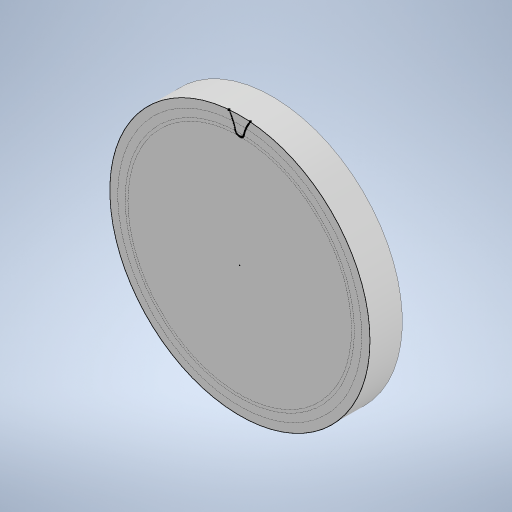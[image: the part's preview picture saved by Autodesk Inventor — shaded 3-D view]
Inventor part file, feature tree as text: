
AUTODESK INVENTOR PART (.ipt)
format: ipt  version: 2024 (Build 280153000, 153)  size: 217,088 bytes
history: native  units: mm
features: extrude x1
ambient origin geometry x8: Origin, YZ Plane, XZ Plane, XY Plane, X Axis, Y Axis, Z Axis, Center Point
bodies: Solid1 (feature_tree)
feature tree (1):
  extrude  "Extrusion1"  Depth=20.0mm
